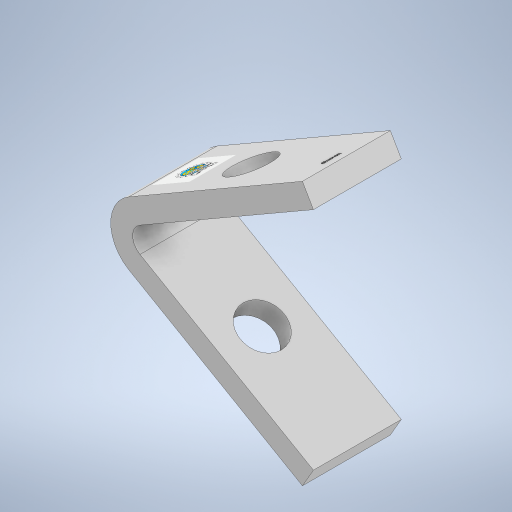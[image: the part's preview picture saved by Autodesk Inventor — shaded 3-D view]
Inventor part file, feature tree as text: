
AUTODESK INVENTOR PART (.ipt)
format: ipt  version: 2023 (Build 270158000, 158)  size: 544,256 bytes
history: native  units: mm
features: sketch x5, hole x2, other x2, extrude x1, emboss x1
ambient origin geometry x8: Origin, YZ Plane, XZ Plane, XY Plane, X Axis, Y Axis, Z Axis, Center Point
bodies: Solid1 (feature_tree)
feature tree (11):
  extrude  "Extrusion1"  Depth=180.0mm
  hole  "Hole1"  [1 undecoded]
  hole  "Hole2"  [1 undecoded]
  emboss  "Emboss3"
  other  "Decal3"
  sketch  "Sketch1"  dims[d0=180.0mm d2=180.0mm]
  sketch  "Sketch2"  dims[d4=25.0mm d5=15.0mm]
  sketch  "Sketch3"  dims[d7=60.0deg d8=60.0mm d9=0.0mm]
  sketch  "Sketch8"  dims[d10=30.0mm]
  sketch  "Sketch9"  dims[d12=30.0mm d13=30.0mm d14=6.0mm d15=4.0mm d16=2.0mm d17=90.0deg d18=16.0mm d19=20.594885mm d20=30.0mm d21=75.0mm d22=30.0mm d23=30.0mm d24=6.0mm d25=4.0mm d26=2.0mm d27=90.0deg d28=16.0mm d29=20.594885mm d91=1.0mm d92=0.0mm d30=0.75mm d31=20.594885mm d32=0.0625mm d33=0.75mm d34=0.375mm]
  other  "Image5"
note: 2 required parameter values undecoded (feature->parameter linkage not recoverable at this tier; creation-order binding heuristic only, values carry confidence <= 0.55)
